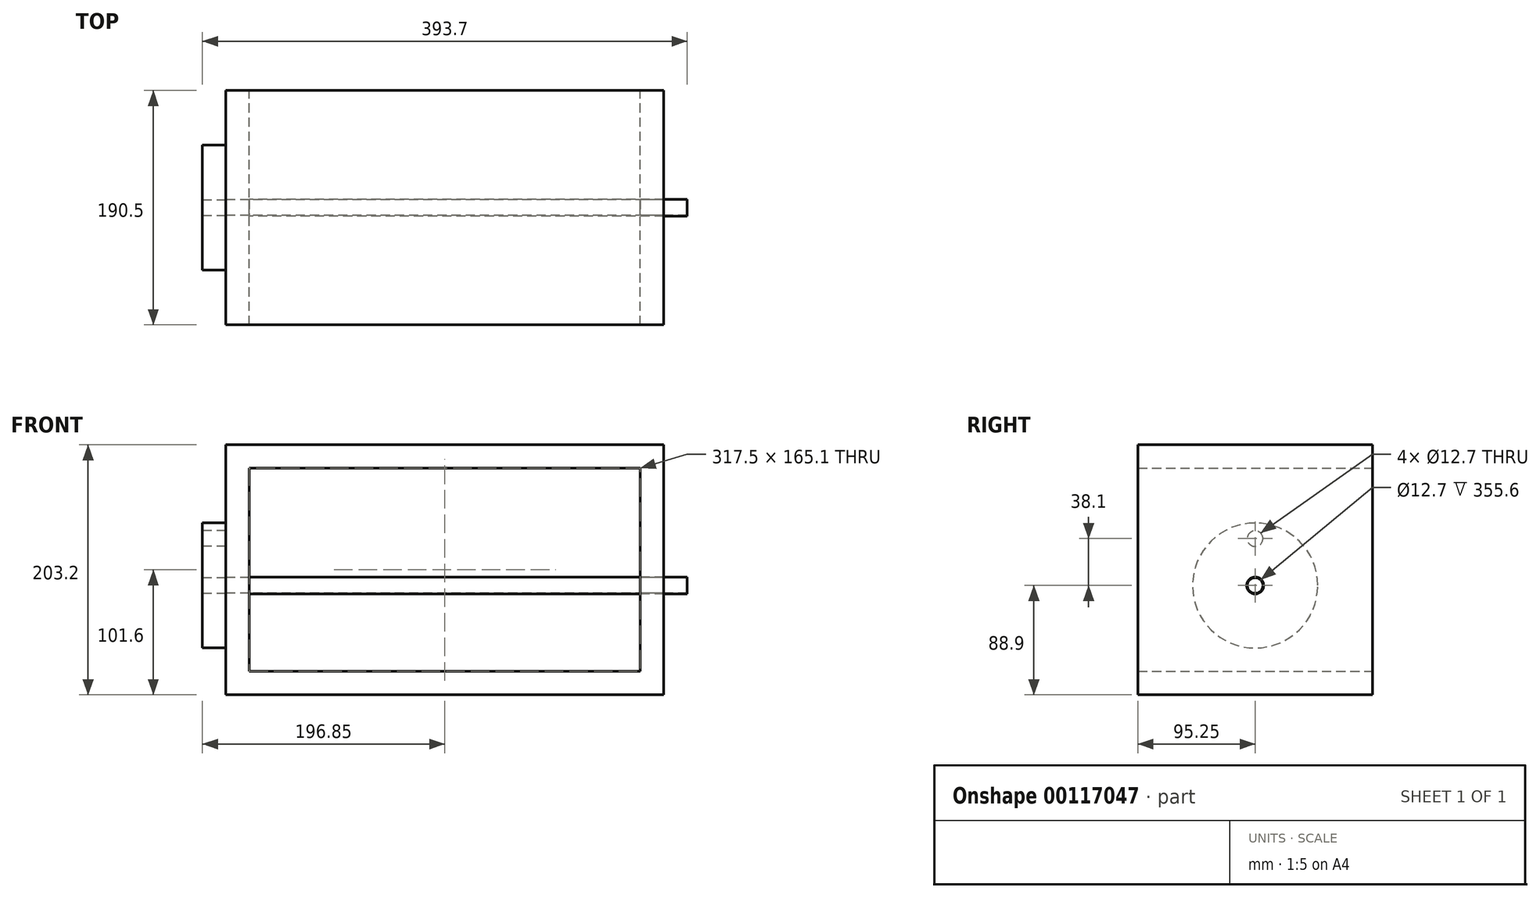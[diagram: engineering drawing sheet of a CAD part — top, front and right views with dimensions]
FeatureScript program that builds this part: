
annotation { "Feature Type Name" : "Feature", "Feature Type Description" : "" }
export const myFeature = defineFeature(function(context is Context, id is Id, definition is map)
    precondition{}
    {
        {
            var Q0;
            Q0=qCreatedBy(makeId("Front.planeOp"),FACE);
            var sketch = newSketch(context, id + "F0", { "sketchPlane" : qUnion([Q0])});
            skLineSegment(sketch, "E0.bottom", {"start": v(158.75, -82.55) * mm, "end": v(-158.75, -82.55) * mm});
            skLineSegment(sketch, "E0.top", {"start": v(158.75, 82.55) * mm, "end": v(-158.75, 82.55) * mm});
            skLineSegment(sketch, "E0.left", {"start": v(158.75, -82.55) * mm, "end": v(158.75, 82.55) * mm});
            skLineSegment(sketch, "E0.right", {"start": v(-158.75, -82.55) * mm, "end": v(-158.75, 82.55) * mm});
            skPoint(sketch, "E0.middle", {"position": v(0, 0) * mm});
            skLineSegment(sketch, "E1.bottom", {"start": v(177.8, -101.6) * mm, "end": v(-177.8, -101.6) * mm});
            skLineSegment(sketch, "E1.top", {"start": v(177.8, 101.6) * mm, "end": v(-177.8, 101.6) * mm});
            skLineSegment(sketch, "E1.left", {"start": v(177.8, -101.6) * mm, "end": v(177.8, 101.6) * mm});
            skLineSegment(sketch, "E1.right", {"start": v(-177.8, -101.6) * mm, "end": v(-177.8, 101.6) * mm});
            skSolve(sketch);
        }
        {
            var Q0;
            Q0 = qSketchRegion(id + "F0", true);
            extrude(context, id + "F1", {"entities" : qUnion([Q0]), "endBound" : BoundingType.SYMMETRIC, "depth" : 190.5 * mm});
        }
        {
            var Q0;
            Q0=makeQuery(id+"F1.opExtrude","SWEPT_FACE",FACE,{"disambiguationData":[OSD([sQuery(id+"F0.wireOp",EDGE,"E1.right")])]});
            var sketch = newSketch(context, id + "F2", { "sketchPlane" : qUnion([Q0])});
            skCircle(sketch, "E2", {"center": v(0, -12.7) * mm, "radius": 6.35 * mm});
            skSolve(sketch);
        }
        {
            var Q0;
            Q0 = qSketchRegion(id + "F2", true);
            extrude(context, id + "F3", {"entities" : qUnion([Q0]), "operationType" : NewBodyOperationType.REMOVE, "endBound" : BoundingType.THROUGH_ALL, "oppositeDirection" : true, "depth" : 25.4 * mm});
        }
        {
            var Q0;
            Q0=makeQuery(id+"F1.opExtrude","SWEPT_FACE",FACE,{"disambiguationData":[OSD([sQuery(id+"F0.wireOp",EDGE,"E1.right")])]});
            var sketch = newSketch(context, id + "F4", { "sketchPlane" : qUnion([Q0])});
            skCircle(sketch, "E3", {"center": v(0, -12.7) * mm, "radius": 50.8 * mm});
            skCircle(sketch, "E4.0", {"center": v(0, -12.7) * mm, "radius": 6.35 * mm});
            skSolve(sketch);
        }
        {
            var Q0;
            Q0 = qSketchRegion(id + "F4", true);
            extrude(context, id + "F5", {"entities" : qUnion([Q0]), "depth" : 19.05 * mm});
        }
        {
            var Q0;
            Q0=makeQuery(id+"F5.opExtrude","CAP_FACE",FACE,{"disambiguationData":[OSD([sQuery(id+"F4.wireOp",EDGE,"E3"),sQuery(id+"F4.wireOp",EDGE,"E4.0")])],"isStart":false});
            var sketch = newSketch(context, id + "F6", { "sketchPlane" : qUnion([Q0])});
            skCircle(sketch, "E5", {"center": v(0, 25.4) * mm, "radius": 6.35 * mm});
            skLineSegment(sketch, "E6", {"start": v(0, -12.7) * mm, "end": v(0, 25.4) * mm, "construction": true});
            skSolve(sketch);
        }
        {
            var Q0;
            Q0 = qSketchRegion(id + "F6", true);
            var Q1;
            Q1=makeQuery(id+"F1.opExtrude","SWEPT_FACE",FACE,{"disambiguationData":[OSD([sQuery(id+"F0.wireOp",EDGE,"E1.right")])]});
            extrude(context, id + "F7", {"entities" : qUnion([Q0]), "operationType" : NewBodyOperationType.REMOVE, "endBound" : BoundingType.UP_TO_SURFACE, "oppositeDirection" : true, "endBoundEntityFace" : qUnion([Q1]), "depth" : 25.4 * mm});
        }
        {
            var Q0;
            Q0=sQuery(id+"F6.wireOp",EDGE,"E5");
            extrude(context, id + "F8", {"bodyType" : ToolBodyType.SURFACE, "surfaceEntities" : qUnion([Q0]), "depth" : 114.3 * mm});
        }
        {
            var Q0;
            Q0=makeQuery(id+"F1.opExtrude","SWEPT_FACE",FACE,{"disambiguationData":[OSD([sQuery(id+"F0.wireOp",EDGE,"E0.right")])]});
            var sketch = newSketch(context, id + "F9", { "sketchPlane" : qUnion([Q0])});
            skCircle(sketch, "E7.0", {"center": v(0, -12.7) * mm, "radius": 6.35 * mm});
            skCircle(sketch, "E8", {"center": v(0, -12.7) * mm, "radius": 6.88 * mm});
            skSolve(sketch);
        }
        {
            var Q0;
            Q0 = qSketchRegion(id + "F9", true);
            extrude(context, id + "F10", {"entities" : qUnion([Q0]), "depth" : 355.6 * mm});
        }
    });
